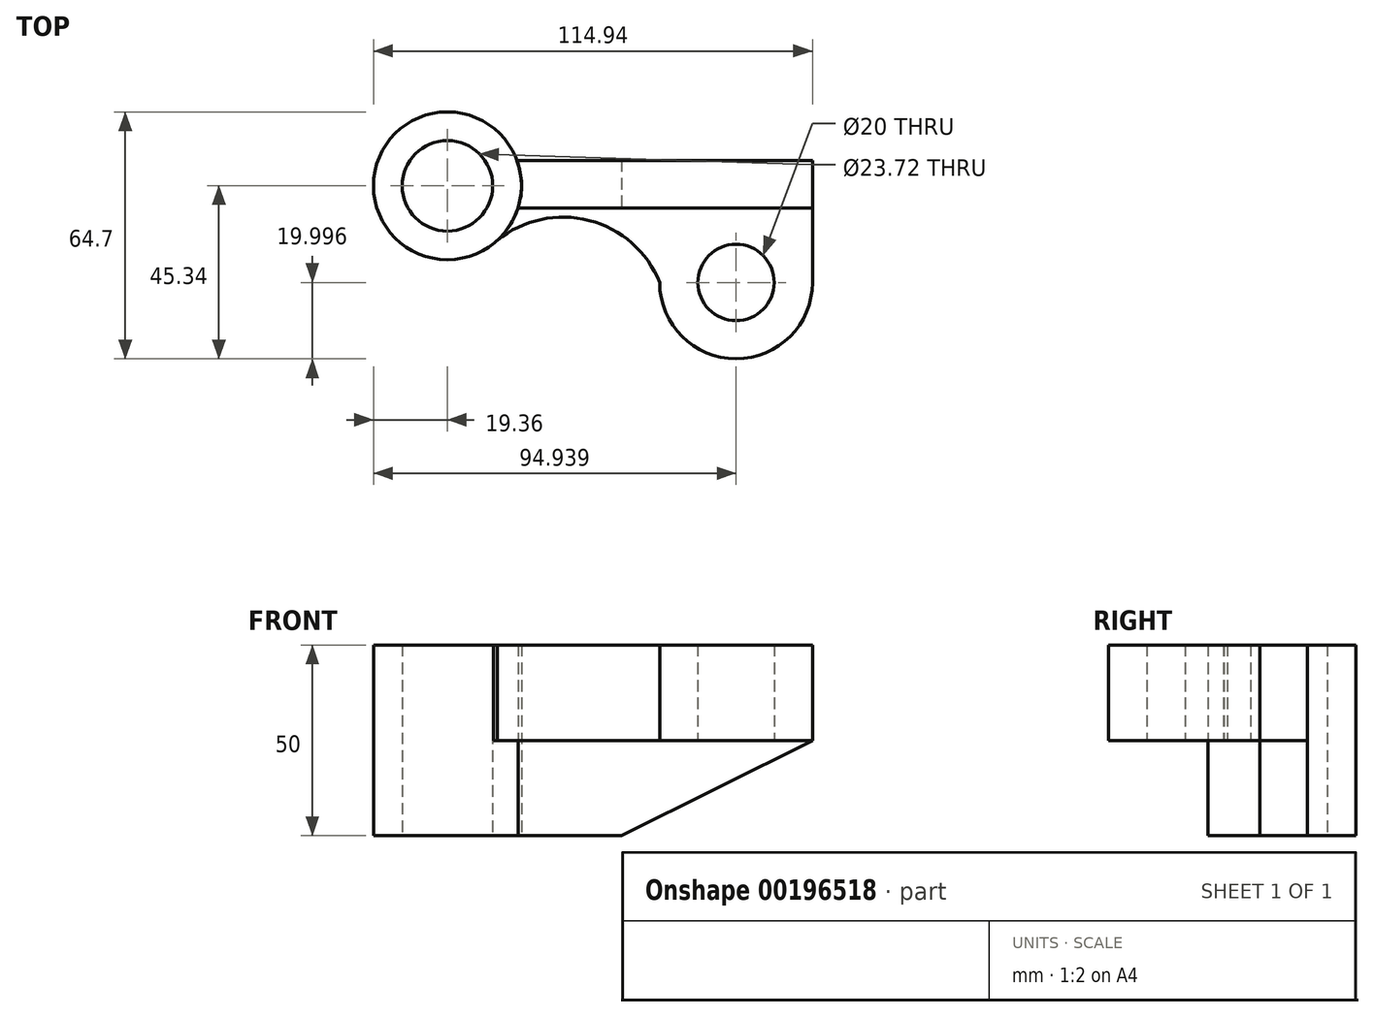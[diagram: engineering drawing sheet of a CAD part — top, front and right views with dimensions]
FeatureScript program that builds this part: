
annotation { "Feature Type Name" : "Feature", "Feature Type Description" : "" }
export const myFeature = defineFeature(function(context is Context, id is Id, definition is map)
    precondition{}
    {
        {
            var Q0;
            Q0=qCreatedBy(makeId("Top.planeOp"),FACE);
            var sketch = newSketch(context, id + "F0", { "sketchPlane" : qUnion([Q0])});
            skCircle(sketch, "E0", {"center": v(0, 0) * mm, "radius": 19.36 * mm});
            skSolve(sketch);
        }
        {
            var Q0;
            Q0 = qSketchRegion(id + "F0", true);
            extrude(context, id + "F1", {"entities" : qUnion([Q0]), "depth" : 50 * mm});
        }
        {
            var Q0;
            Q0=makeQuery(id+"F1.opExtrude","CAP_FACE",FACE,{"disambiguationData":[OSD([sQuery(id+"F0.wireOp",EDGE,"E0")])],"isStart":false});
            var Q1;
            Q1=makeQuery(id+"F1.opExtrude","CAP_FACE",FACE,{"disambiguationData":[OSD([sQuery(id+"F0.wireOp",EDGE,"E0")])],"isStart":true});
            shell(context, id + "F2", {"entities" : qUnion([Q0, Q1]), "thickness" : 7.5 * mm});
        }
        {
            var Q0;
            Q0=makeQuery(id+"F1.opExtrude","CAP_FACE",FACE,{"disambiguationData":[OSD([sQuery(id+"F0.wireOp",EDGE,"E0")])],"isStart":true});
            var sketch = newSketch(context, id + "F3", { "sketchPlane" : qUnion([Q0])});
            skLineSegment(sketch, "E1.bottom", {"start": v(18.48, 5.77) * mm, "end": v(95.58, 5.77) * mm});
            skLineSegment(sketch, "E1.top", {"start": v(18.18, -6.66) * mm, "end": v(95.58, -6.66) * mm});
            skLineSegment(sketch, "E1.right", {"start": v(95.58, 5.77) * mm, "end": v(95.58, -6.66) * mm});
            skArc(sketch, "E2", {"start": v(18.18, -6.66) * mm, "mid": v(19.44, -0.47) * mm, "end": v(18.48, 5.77) * mm});
            skSolve(sketch);
        }
        {
            var Q0;
            Q0 = qSketchRegion(id + "F3", true);
            extrude(context, id + "F4", {"entities" : qUnion([Q0]), "oppositeDirection" : true, "depth" : 50 * mm});
        }
        {
            var Q0;
            Q0=makeQuery(id+"F4.opExtrude","SWEPT_FACE",FACE,{"disambiguationData":[OSD([sQuery(id+"F3.wireOp",EDGE,"E1.bottom")])]});
            var sketch = newSketch(context, id + "F5", { "sketchPlane" : qUnion([Q0])});
            skLineSegment(sketch, "E3", {"start": v(45.58, 0) * mm, "end": v(95.58, 25) * mm});
            skLineSegment(sketch, "E4", {"start": v(95.58, 25) * mm, "end": v(95.58, 0) * mm});
            skLineSegment(sketch, "E5", {"start": v(95.58, 0) * mm, "end": v(45.58, 0) * mm});
            skSolve(sketch);
        }
        {
            var Q0;
            Q0 = qSketchRegion(id + "F5", true);
            extrude(context, id + "F6", {"entities" : qUnion([Q0]), "operationType" : NewBodyOperationType.REMOVE, "oppositeDirection" : true, "depth" : 25 * mm});
        }
        {
            var Q0;
            Q0=qCreatedBy(makeId("Top.planeOp"),FACE);
            var sketch = newSketch(context, id + "F7", { "sketchPlane" : qUnion([Q0])});
            skArc(sketch, "E6", {"start": v(12.09, -15.13) * mm, "mid": v(16, -10.93) * mm, "end": v(18.48, -5.77) * mm});
            skLineSegment(sketch, "E7", {"start": v(95.58, -5.77) * mm, "end": v(18.48, -5.77) * mm});
            skArc(sketch, "E8", {"start": v(55.58, -25.34) * mm, "mid": v(75.58, -45.34) * mm, "end": v(95.58, -25.34) * mm});
            skLineSegment(sketch, "E9", {"start": v(95.58, -25.34) * mm, "end": v(95.58, -5.77) * mm});
            skArc(sketch, "E10", {"start": v(55.58, -25.34) * mm, "mid": v(36.49, -8.93) * mm, "end": v(12.09, -15.13) * mm});
            skCircle(sketch, "E11", {"center": v(75.58, -25.34) * mm, "radius": 10 * mm});
            skSolve(sketch);
        }
        {
            var Q0;
            Q0 = qSketchRegion(id + "F7", true);
            extrude(context, id + "F8", {"entities" : qUnion([Q0]), "depth" : 50 * mm, "hasSecondDirection" : true, "secondDirectionOppositeDirection" : false, "secondDirectionDepth" : 25 * mm});
        }
    });
